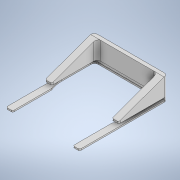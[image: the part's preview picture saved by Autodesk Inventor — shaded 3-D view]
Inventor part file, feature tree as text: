
AUTODESK INVENTOR PART (.ipt)
format: ipt  version: 2020 (Build 240168000, 168)  size: 224,768 bytes
history: native  units: in
note: dims shown in document units (in); Inventor stores cm internally (conversion verified against a paired STEP export)
features: extrude x8, sketch x8, fillet x5
ambient origin geometry x8: Origin, YZ Plane, XZ Plane, XY Plane, X Axis, Y Axis, Z Axis, Center Point
bodies: Solid1 (feature_tree)
feature tree (21):
  extrude  "Extrusion1"  Depth=4.7244in
  extrude  "Extrusion2"  TaperAngle=0.0deg  [1 undecoded]
  extrude  "Extrusion7"  Depth=3.5039in
  extrude  "Extrusion8"  Depth=0.2126in TaperAngle=0.0deg
  extrude  "Extrusion9"  Depth=3.5827in TaperAngle=0.0deg
  extrude  "Extrusion10"  Depth=0.1969in
  fillet  "Fillet1"  Radius=0.1969in
  fillet  "Fillet2"  Radius=0.0787in
  fillet  "Fillet3"  Radius=0.0787in
  fillet  "Fillet4"  Radius=0.3307in
  extrude  "Extrusion11"  Depth=0.3307in TaperAngle=0.0deg
  extrude  "Extrusion12"  Depth=0.0787in
  fillet  "Fillet5"  Radius=0.1654in
  sketch  "Sketch1"  dims[d0=3.937in d1=4.7244in]
  sketch  "Sketch2"  dims[d2=1.1811in d3=0.0in d9=0.0in d10=0.0in]
  sketch  "Sketch11"  dims[d23=4.5276in d24=3.5039in]
  sketch  "Sketch13"  dims[d25=1.752in d26=0.2126in d27=0.0in]
  sketch  "Sketch14"  dims[d28=3.5827in d29=0.0in d30=3.5827in d31=0.0in]
  sketch  "Sketch15"  dims[d32=1.9685in d33=0.0in d34=0.1969in d35=0.1969in d36=0.0787in d37=0.0787in d38=0.3307in]
  sketch  "Sketch16"  dims[d39=0.1181in d40=0.3307in d41=0.0in]
  sketch  "Sketch17"  dims[d42=0.2126in d43=0.1654in d44=0.1654in d45=0.0in d46=0.0in d47=0.0787in d4=0.0197in d5=0.0344in]
note: 1 required parameter value undecoded (feature->parameter linkage not recoverable at this tier; creation-order binding heuristic only, values carry confidence <= 0.55)
